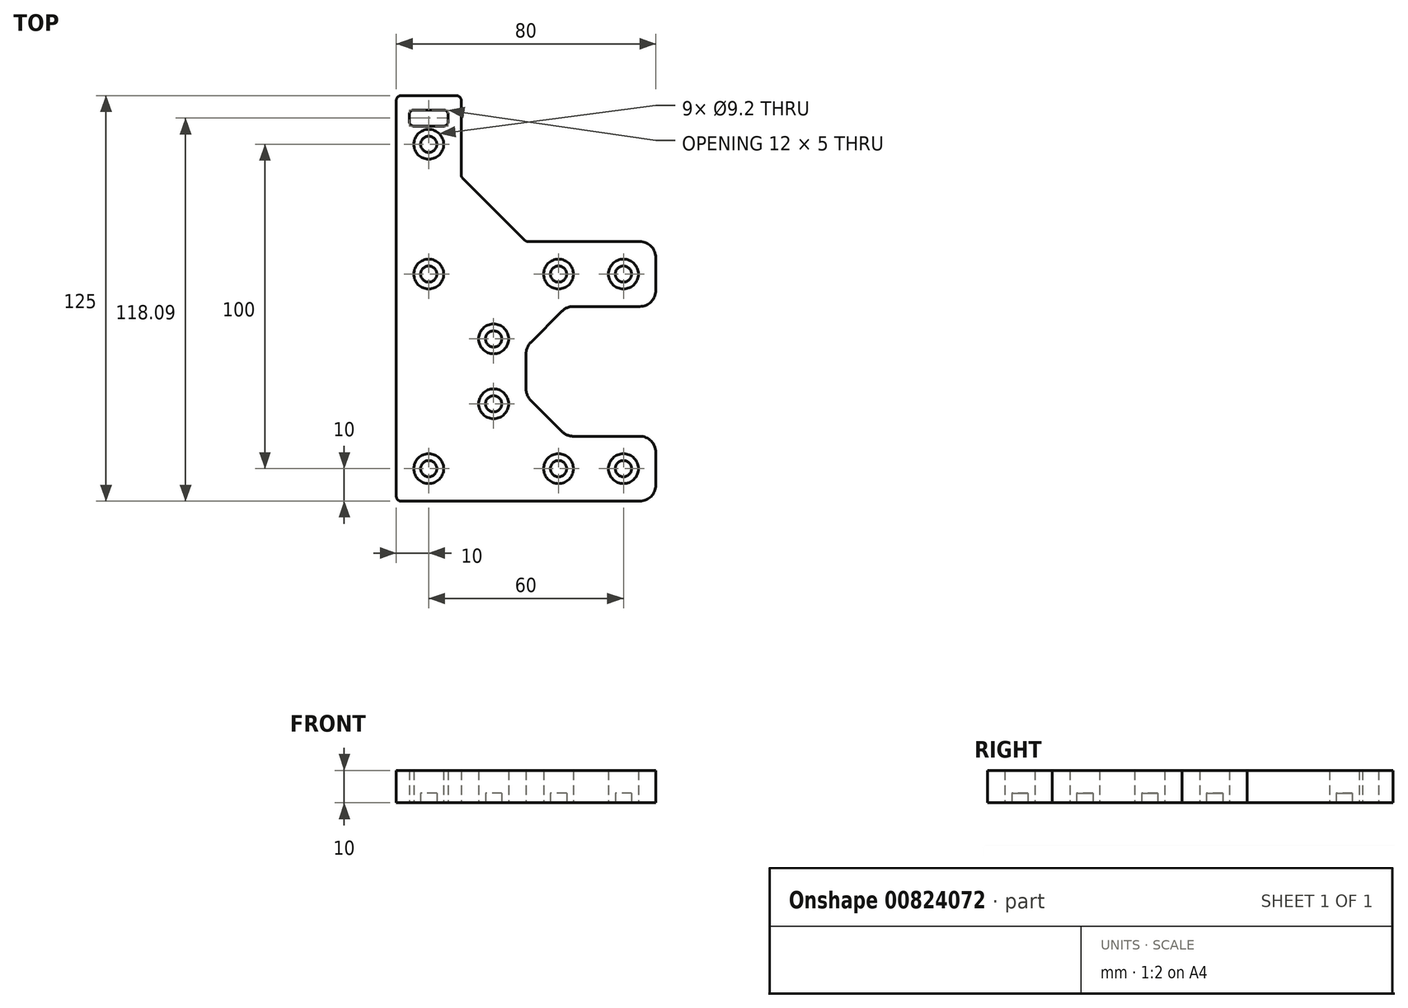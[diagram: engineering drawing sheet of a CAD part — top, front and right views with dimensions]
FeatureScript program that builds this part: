
annotation { "Feature Type Name" : "Feature", "Feature Type Description" : "" }
export const myFeature = defineFeature(function(context is Context, id is Id, definition is map)
    precondition{}
    {
        {
            var Q0;
            Q0=qCreatedBy(makeId("Top.planeOp"),FACE);
            var sketch = newSketch(context, id + "F0", { "sketchPlane" : qUnion([Q0])});
            skLineSegment(sketch, "E0", {"start": v(-38.5, -62.5) * mm, "end": v(35, -62.5) * mm});
            skLineSegment(sketch, "E1", {"start": v(-40, 61) * mm, "end": v(-40, -61) * mm});
            skLineSegment(sketch, "E2", {"start": v(35, -42.5) * mm, "end": v(14.57, -42.5) * mm});
            skLineSegment(sketch, "E3", {"start": v(-36, 56.65) * mm, "end": v(-36, 54.53) * mm});
            skLineSegment(sketch, "E4", {"start": v(-24, 54.53) * mm, "end": v(-24, 56.65) * mm});
            skLineSegment(sketch, "E5", {"start": v(-20, 61) * mm, "end": v(-20, 38.12) * mm});
            skLineSegment(sketch, "E6", {"start": v(1.46, -31.46) * mm, "end": v(11.04, -41.04) * mm});
            skLineSegment(sketch, "E7", {"start": v(0, -17.07) * mm, "end": v(0, -27.93) * mm});
            skLineSegment(sketch, "E8", {"start": v(35, -2.5) * mm, "end": v(14.57, -2.5) * mm});
            skLineSegment(sketch, "E9", {"start": v(11.04, -3.96) * mm, "end": v(1.46, -13.54) * mm});
            skLineSegment(sketch, "E10", {"start": v(-19.56, 37.06) * mm, "end": v(-0.44, 17.94) * mm});
            skLineSegment(sketch, "E11", {"start": v(35, 17.5) * mm, "end": v(0.62, 17.5) * mm});
            skLineSegment(sketch, "E12", {"start": v(40, -57.5) * mm, "end": v(40, -47.5) * mm});
            skLineSegment(sketch, "E13", {"start": v(40, 2.5) * mm, "end": v(40, 12.5) * mm});
            skLineSegment(sketch, "E14", {"start": v(-34.56, 53.1) * mm, "end": v(-25.44, 53.1) * mm});
            skLineSegment(sketch, "E15", {"start": v(-25.44, 58.1) * mm, "end": v(-34.56, 58.1) * mm});
            skLineSegment(sketch, "E16", {"start": v(-21.5, 62.5) * mm, "end": v(-38.5, 62.5) * mm});
            skArc(sketch, "E17", {"start": v(11.04, -41.04) * mm, "mid": v(12.66, -42.12) * mm, "end": v(14.57, -42.5) * mm});
            skArc(sketch, "E18", {"start": v(0, -27.93) * mm, "mid": v(0.38, -29.84) * mm, "end": v(1.46, -31.46) * mm});
            skArc(sketch, "E19", {"start": v(1.46, -13.54) * mm, "mid": v(0.38, -15.16) * mm, "end": v(0, -17.07) * mm});
            skArc(sketch, "E20", {"start": v(14.57, -2.5) * mm, "mid": v(12.66, -2.88) * mm, "end": v(11.04, -3.96) * mm});
            skArc(sketch, "E21", {"start": v(35, -62.5) * mm, "mid": v(38.54, -61.04) * mm, "end": v(40, -57.5) * mm});
            skArc(sketch, "E22", {"start": v(40, -47.5) * mm, "mid": v(38.54, -43.96) * mm, "end": v(35, -42.5) * mm});
            skArc(sketch, "E23", {"start": v(40, 12.5) * mm, "mid": v(38.54, 16.04) * mm, "end": v(35, 17.5) * mm});
            skArc(sketch, "E24", {"start": v(35, -2.5) * mm, "mid": v(38.54, -1.04) * mm, "end": v(40, 2.5) * mm});
            skCircle(sketch, "E25", {"center": v(-30, 7.5) * mm, "radius": 2.5 * mm});
            skCircle(sketch, "E26", {"center": v(-10, -32.5) * mm, "radius": 2.5 * mm});
            skCircle(sketch, "E27", {"center": v(-10, -12.5) * mm, "radius": 2.5 * mm});
            skCircle(sketch, "E28", {"center": v(10, 7.5) * mm, "radius": 2.5 * mm});
            skCircle(sketch, "E29", {"center": v(30, 7.5) * mm, "radius": 2.5 * mm});
            skCircle(sketch, "E30", {"center": v(30, -52.5) * mm, "radius": 2.5 * mm});
            skCircle(sketch, "E31", {"center": v(10, -52.5) * mm, "radius": 2.5 * mm});
            skCircle(sketch, "E32", {"center": v(-30, -52.5) * mm, "radius": 2.5 * mm});
            skCircle(sketch, "E33", {"center": v(-30, 47.5) * mm, "radius": 2.5 * mm});
            skArc(sketch, "E34", {"start": v(-20, 38.12) * mm, "mid": v(-19.89, 37.55) * mm, "end": v(-19.56, 37.06) * mm});
            skArc(sketch, "E35", {"start": v(-0.44, 17.94) * mm, "mid": v(0.05, 17.61) * mm, "end": v(0.62, 17.5) * mm});
            skArc(sketch, "E36", {"start": v(-20, 61) * mm, "mid": v(-20.44, 62.06) * mm, "end": v(-21.5, 62.5) * mm});
            skArc(sketch, "E37", {"start": v(-38.5, 62.5) * mm, "mid": v(-39.56, 62.06) * mm, "end": v(-40, 61) * mm});
            skArc(sketch, "E38", {"start": v(-40, -61) * mm, "mid": v(-39.56, -62.06) * mm, "end": v(-38.5, -62.5) * mm});
            skArc(sketch, "E39", {"start": v(-34.56, 58.1) * mm, "mid": v(-35.58, 57.67) * mm, "end": v(-36, 56.65) * mm});
            skArc(sketch, "E40", {"start": v(-24, 56.65) * mm, "mid": v(-24.42, 57.67) * mm, "end": v(-25.44, 58.1) * mm});
            skArc(sketch, "E41", {"start": v(-25.44, 53.1) * mm, "mid": v(-24.42, 53.51) * mm, "end": v(-24, 54.53) * mm});
            skArc(sketch, "E42", {"start": v(-36, 54.53) * mm, "mid": v(-35.58, 53.51) * mm, "end": v(-34.56, 53.1) * mm});
            skCircle(sketch, "E43.0", {"center": v(-30, -52.5) * mm, "radius": 4.6 * mm});
            skCircle(sketch, "E44.0", {"center": v(10, -52.5) * mm, "radius": 4.6 * mm});
            skCircle(sketch, "E45.0", {"center": v(30, -52.5) * mm, "radius": 4.6 * mm});
            skCircle(sketch, "E46.0", {"center": v(-10, -32.5) * mm, "radius": 4.6 * mm});
            skCircle(sketch, "E47.0", {"center": v(-10, -12.5) * mm, "radius": 4.6 * mm});
            skCircle(sketch, "E48.0", {"center": v(-30, 7.5) * mm, "radius": 4.6 * mm});
            skCircle(sketch, "E49.0", {"center": v(10, 7.5) * mm, "radius": 4.6 * mm});
            skCircle(sketch, "E50.0", {"center": v(30, 7.5) * mm, "radius": 4.6 * mm});
            skCircle(sketch, "E51.0", {"center": v(-30, 47.5) * mm, "radius": 4.6 * mm});
            skSolve(sketch);
        }
        {
            var Q0;
            Q0=qSketchRegion(id+"F0",true);
            extrude(context, id + "F1", {"entities" : qUnion([Q0]), "depth" : 10 * mm, "offsetDistance" : 25 * mm});
        }
        {
            var Q0;
            Q0=makeQuery(id+"F0.imprint","IMPRINT",FACE,{"disambiguationData":[TD([[makeQuery(id+"F0.imprint","IMPRINT",EDGE,{"derivedFrom":sQuery(id+"F0.wireOp",EDGE,"E33")}),1.0]])]});
            var Q1;
            Q1=makeQuery(id+"F0.imprint","IMPRINT",FACE,{"disambiguationData":[TD([[makeQuery(id+"F0.imprint","IMPRINT",EDGE,{"derivedFrom":sQuery(id+"F0.wireOp",EDGE,"E25")}),1.0]])]});
            var Q2;
            Q2=makeQuery(id+"F0.imprint","IMPRINT",FACE,{"disambiguationData":[TD([[makeQuery(id+"F0.imprint","IMPRINT",EDGE,{"derivedFrom":sQuery(id+"F0.wireOp",EDGE,"E32")}),1.0]])]});
            var Q3;
            Q3=makeQuery(id+"F0.imprint","IMPRINT",FACE,{"disambiguationData":[TD([[makeQuery(id+"F0.imprint","IMPRINT",EDGE,{"derivedFrom":sQuery(id+"F0.wireOp",EDGE,"E26")}),1.0]])]});
            var Q4;
            Q4=makeQuery(id+"F0.imprint","IMPRINT",FACE,{"disambiguationData":[TD([[makeQuery(id+"F0.imprint","IMPRINT",EDGE,{"derivedFrom":sQuery(id+"F0.wireOp",EDGE,"E31")}),1.0]])]});
            var Q5;
            Q5=makeQuery(id+"F0.imprint","IMPRINT",FACE,{"disambiguationData":[TD([[makeQuery(id+"F0.imprint","IMPRINT",EDGE,{"derivedFrom":sQuery(id+"F0.wireOp",EDGE,"E30")}),1.0]])]});
            var Q6;
            Q6=makeQuery(id+"F0.imprint","IMPRINT",FACE,{"disambiguationData":[TD([[makeQuery(id+"F0.imprint","IMPRINT",EDGE,{"derivedFrom":sQuery(id+"F0.wireOp",EDGE,"E27")}),1.0]])]});
            var Q7;
            Q7=makeQuery(id+"F0.imprint","IMPRINT",FACE,{"disambiguationData":[TD([[makeQuery(id+"F0.imprint","IMPRINT",EDGE,{"derivedFrom":sQuery(id+"F0.wireOp",EDGE,"E28")}),1.0]])]});
            var Q8;
            Q8=makeQuery(id+"F0.imprint","IMPRINT",FACE,{"disambiguationData":[TD([[makeQuery(id+"F0.imprint","IMPRINT",EDGE,{"derivedFrom":sQuery(id+"F0.wireOp",EDGE,"E29")}),1.0]])]});
            extrude(context, id + "F2", {"entities" : qUnion([Q0, Q1, Q2, Q3, Q4, Q5, Q6, Q7, Q8]), "operationType" : NewBodyOperationType.ADD, "depth" : 3 * mm, "offsetDistance" : 25 * mm});
        }
    });
